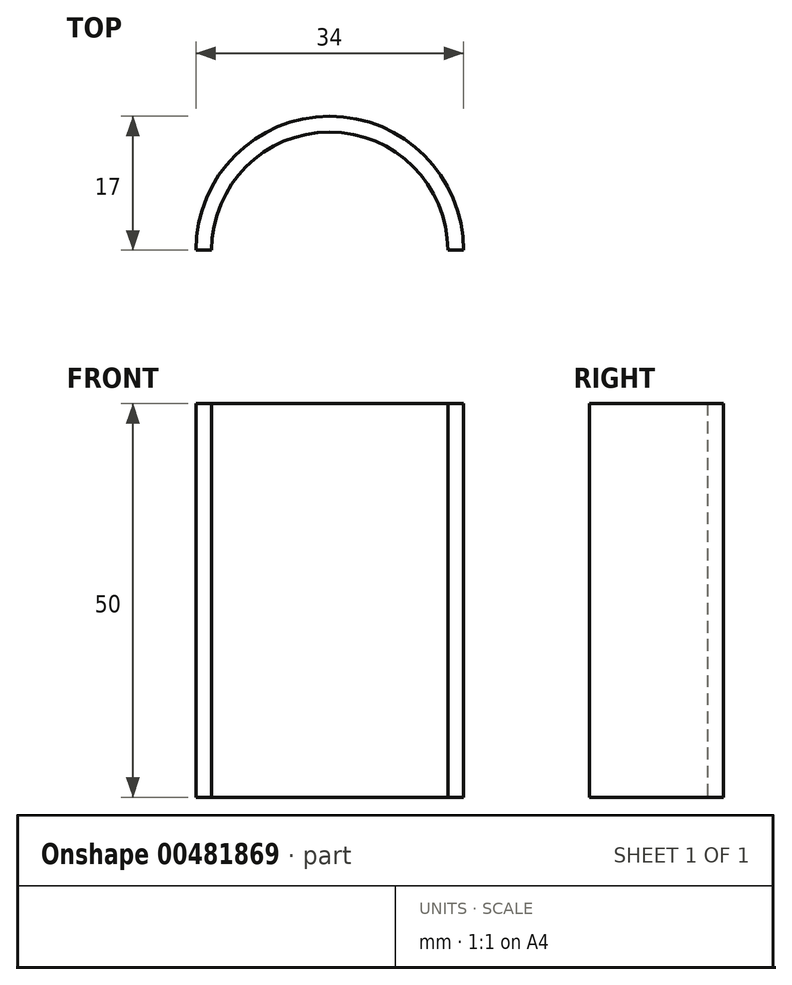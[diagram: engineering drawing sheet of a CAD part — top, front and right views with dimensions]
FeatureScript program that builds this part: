
annotation { "Feature Type Name" : "Feature", "Feature Type Description" : "" }
export const myFeature = defineFeature(function(context is Context, id is Id, definition is map)
    precondition{}
    {
        {
            var Q0;
            Q0=qCreatedBy(makeId("Top.planeOp"),FACE);
            var sketch = newSketch(context, id + "F0", { "sketchPlane" : qUnion([Q0])});
            skArc(sketch, "E0", {"start": v(40.62, 0) * mm, "mid": v(25.62, 15) * mm, "end": v(10.62, 0) * mm});
            skLineSegment(sketch, "E1", {"start": v(10.62, 0) * mm, "end": v(8.62, 0) * mm});
            skLineSegment(sketch, "E2", {"start": v(40.62, 0) * mm, "end": v(42.62, 0) * mm});
            skArc(sketch, "E3", {"start": v(42.62, 0) * mm, "mid": v(25.62, 17) * mm, "end": v(8.62, 0) * mm});
            skSolve(sketch);
        }
        {
            var Q0;
            Q0=makeQuery(id+"F0.imprint","IMPRINT",FACE,{"disambiguationData":[TD([[makeQuery(id+"F0.imprint","IMPRINT",EDGE,{"derivedFrom":sQuery(id+"F0.wireOp",EDGE,"E0")}),-1.0]])]});
            extrude(context, id + "F1", {"entities" : qUnion([Q0]), "depth" : 50 * mm});
        }
    });
